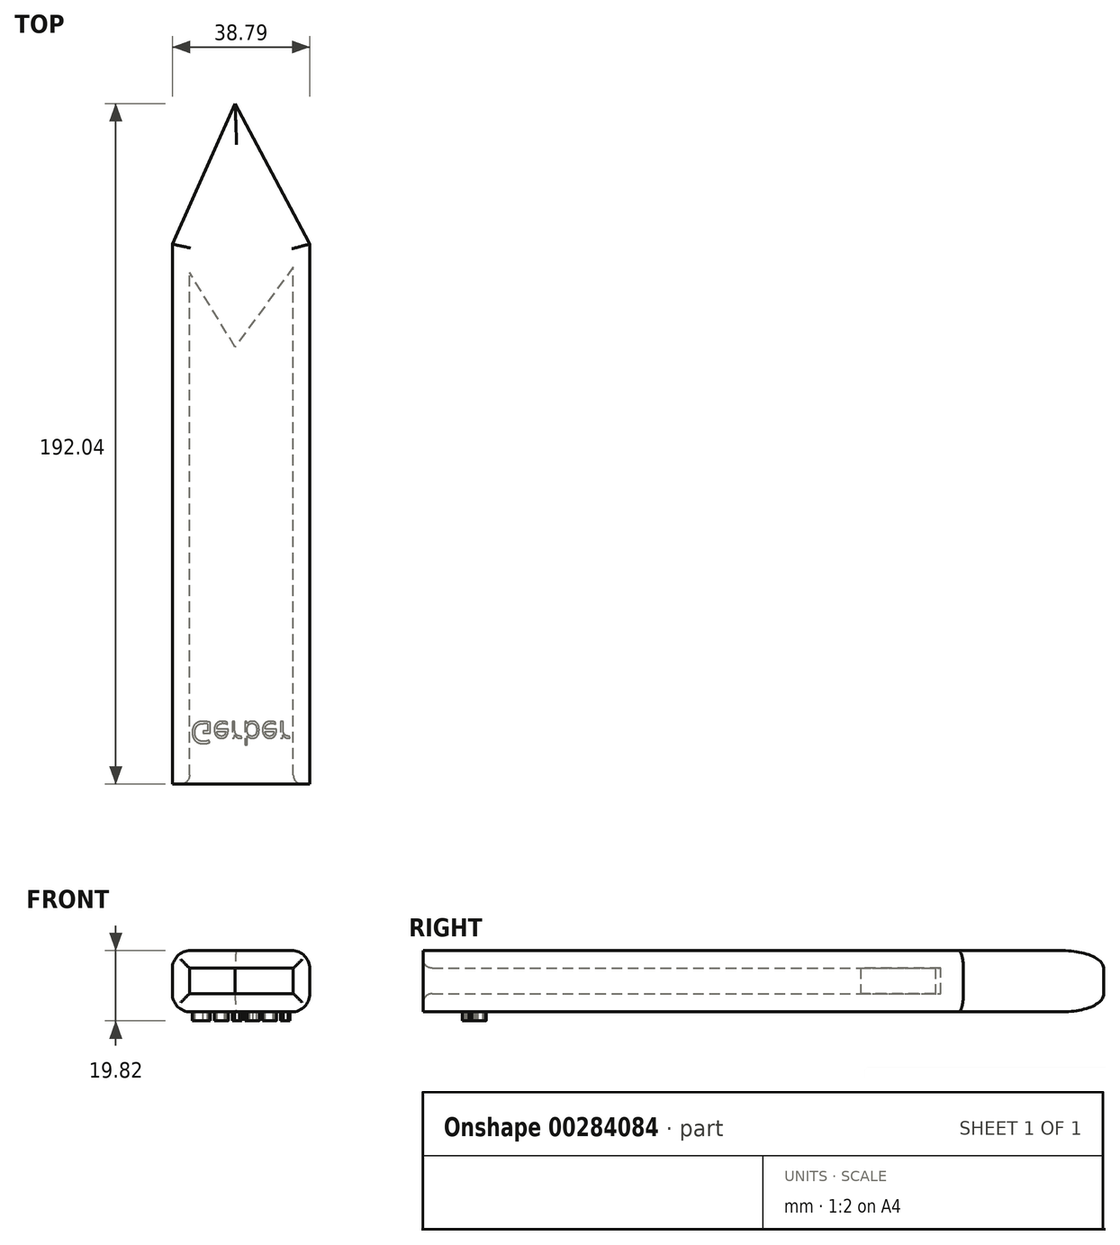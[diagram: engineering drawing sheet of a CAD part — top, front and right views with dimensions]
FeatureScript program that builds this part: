
annotation { "Feature Type Name" : "Feature", "Feature Type Description" : "" }
export const myFeature = defineFeature(function(context is Context, id is Id, definition is map)
    precondition{}
    {
        {
            var Q0;
            Q0=qCreatedBy(makeId("Front.planeOp"),FACE);
            var sketch = newSketch(context, id + "F0", { "sketchPlane" : qUnion([Q0])});
            skLineSegment(sketch, "E0", {"start": v(-12.88, 15.66) * mm, "end": v(16.4, 15.66) * mm});
            skLineSegment(sketch, "E1", {"start": v(16.4, 15.66) * mm, "end": v(16.4, 8.49) * mm});
            skLineSegment(sketch, "E2", {"start": v(16.4, 8.49) * mm, "end": v(-12.88, 8.49) * mm});
            skLineSegment(sketch, "E3", {"start": v(-12.88, 8.49) * mm, "end": v(-12.88, 15.66) * mm});
            skLineSegment(sketch, "E4", {"start": v(-17.73, 20.6) * mm, "end": v(-17.73, 3.33) * mm});
            skLineSegment(sketch, "E5", {"start": v(-17.73, 3.33) * mm, "end": v(21.06, 3.33) * mm});
            skLineSegment(sketch, "E6", {"start": v(-17.73, 20.6) * mm, "end": v(21.06, 20.6) * mm});
            skLineSegment(sketch, "E7", {"start": v(21.06, 3.33) * mm, "end": v(21.06, 20.6) * mm});
            skSolve(sketch);
        }
        {
            var Q0;
            Q0 = qSketchRegion(id + "F0", true);
            extrude(context, id + "F1", {"entities" : qUnion([Q0]), "depth" : 152.4 * mm});
        }
        {
            var Q0;
            Q0=makeQuery(id+"F1.opExtrude","CAP_EDGE",EDGE,{"disambiguationData":[OSD([sQuery(id+"F0.wireOp",EDGE,"E2")])],"isStart":false});
            var Q1;
            Q1=makeQuery(id+"F1.opExtrude","CAP_EDGE",EDGE,{"disambiguationData":[OSD([sQuery(id+"F0.wireOp",EDGE,"E1")])],"isStart":false});
            var Q2;
            Q2=makeQuery(id+"F1.opExtrude","CAP_EDGE",EDGE,{"disambiguationData":[OSD([sQuery(id+"F0.wireOp",EDGE,"E0")])],"isStart":false});
            var Q3;
            Q3=makeQuery(id+"F1.opExtrude","CAP_EDGE",EDGE,{"disambiguationData":[OSD([sQuery(id+"F0.wireOp",EDGE,"E3")])],"isStart":false});
            fillet(context, id + "F2", {"entities" : qUnion([Q0, Q1, Q2, Q3]), "radius" : 2.54 * mm, "tangentPropagation" : true, "allowEdgeOverflow" : false});
        }
        {
            var Q0;
            Q0=makeQuery(id+"F1.opExtrude","CAP_FACE",FACE,{"disambiguationData":[OSD([sQuery(id+"F0.wireOp",EDGE,"E0"),sQuery(id+"F0.wireOp",EDGE,"E1"),sQuery(id+"F0.wireOp",EDGE,"E2"),sQuery(id+"F0.wireOp",EDGE,"E3"),sQuery(id+"F0.wireOp",EDGE,"E4"),sQuery(id+"F0.wireOp",EDGE,"E5"),sQuery(id+"F0.wireOp",EDGE,"E6"),sQuery(id+"F0.wireOp",EDGE,"E7")])],"isStart":true});
            var sketch = newSketch(context, id + "F3", { "sketchPlane" : qUnion([Q0])});
            skLineSegment(sketch, "E8", {"start": v(12.65, 3.33) * mm, "end": v(12.65, 20.6) * mm});
            skLineSegment(sketch, "E9", {"start": v(12.65, 20.6) * mm, "end": v(-15.98, 20.6) * mm});
            skLineSegment(sketch, "E10", {"start": v(-15.98, 20.6) * mm, "end": v(-15.98, 3.33) * mm});
            skLineSegment(sketch, "E11", {"start": v(-15.98, 3.33) * mm, "end": v(12.65, 3.33) * mm});
            skSolve(sketch);
        }
        {
            var Q0;
            Q0 = qSketchRegion(id + "F3", true);
            extrude(context, id + "F4", {"entities" : qUnion([Q0]), "operationType" : NewBodyOperationType.ADD, "oppositeDirection" : true, "depth" : 0.5 * mm});
        }
        {
            var Q0;
            Q0=makeQuery(id+"F1.opExtrude","SWEPT_FACE",FACE,{"disambiguationData":[OSD([sQuery(id+"F0.wireOp",EDGE,"E5")])]});
            var sketch = newSketch(context, id + "F5", { "sketchPlane" : qUnion([Q0])});
            skLineSegment(sketch, "E12", {"start": v(-17.73, 0) * mm, "end": v(0, -39.64) * mm});
            skLineSegment(sketch, "E13", {"start": v(0, -39.64) * mm, "end": v(21.06, 0) * mm});
            skLineSegment(sketch, "E14", {"start": v(-17.73, 0) * mm, "end": v(0, 29) * mm});
            skLineSegment(sketch, "E15", {"start": v(0, 29) * mm, "end": v(21.06, 0) * mm});
            skSolve(sketch);
        }
        {
            var Q0;
            Q0 = qSketchRegion(id + "F5", true);
            extrude(context, id + "F6", {"entities" : qUnion([Q0]), "operationType" : NewBodyOperationType.ADD, "oppositeDirection" : true, "depth" : 17.27 * mm});
        }
        {
            var Q0;
            Q0=makeQuery(id+"F6.opExtrude","CAP_EDGE",EDGE,{"disambiguationData":[OSD([sQuery(id+"F5.wireOp",EDGE,"E12")])],"isStart":true});
            var Q1;
            Q1=makeQuery(id+"F6.opExtrude","CAP_EDGE",EDGE,{"disambiguationData":[OSD([sQuery(id+"F5.wireOp",EDGE,"E13")])],"isStart":true});
            var Q2;
            Q2=makeQuery(id+"F1.opExtrude","SWEPT_EDGE",EDGE,{"disambiguationData":[OSD([sQuery(id+"F0.wireOp",EDGE,"E5"),sQuery(id+"F0.wireOp",EDGE,"E7")])]});
            var Q3;
            Q3=makeQuery(id+"F1.opExtrude","SWEPT_EDGE",EDGE,{"disambiguationData":[OSD([sQuery(id+"F0.wireOp",EDGE,"E4"),sQuery(id+"F0.wireOp",EDGE,"E5")])]});
            fillet(context, id + "F7", {"entities" : qUnion([Q0, Q1, Q2, Q3]), "radius" : 5.08 * mm, "tangentPropagation" : true, "allowEdgeOverflow" : false});
        }
        {
            var Q0;
            Q0=makeQuery(id+"F1.opExtrude","SWEPT_EDGE",EDGE,{"disambiguationData":[OSD([sQuery(id+"F0.wireOp",EDGE,"E6"),sQuery(id+"F0.wireOp",EDGE,"E7")])]});
            var Q1;
            Q1=makeQuery(id+"F6.opExtrude","CAP_EDGE",EDGE,{"disambiguationData":[OSD([sQuery(id+"F5.wireOp",EDGE,"E13")])],"isStart":false});
            var Q2;
            Q2=makeQuery(id+"F6.opExtrude","CAP_EDGE",EDGE,{"disambiguationData":[OSD([sQuery(id+"F5.wireOp",EDGE,"E12")])],"isStart":false});
            var Q3;
            Q3=makeQuery(id+"F1.opExtrude","SWEPT_EDGE",EDGE,{"disambiguationData":[OSD([sQuery(id+"F0.wireOp",EDGE,"E4"),sQuery(id+"F0.wireOp",EDGE,"E6")])]});
            fillet(context, id + "F8", {"entities" : qUnion([Q0, Q1, Q2, Q3]), "radius" : 5.08 * mm, "tangentPropagation" : true, "allowEdgeOverflow" : false});
        }
        {
            var Q0;
            Q0=makeQuery(id+"F6.boolean.opBoolean","MERGE",FACE,{"derivedFrom":[makeQuery(id+"F1.opExtrude","SWEPT_FACE",FACE,{"disambiguationData":[OSD([sQuery(id+"F0.wireOp",EDGE,"E5")])]}),makeQuery(id+"F6.opExtrude","CAP_FACE",FACE,{"disambiguationData":[OSD([sQuery(id+"F5.wireOp",EDGE,"E12"),sQuery(id+"F5.wireOp",EDGE,"E13"),sQuery(id+"F5.wireOp",EDGE,"E14"),sQuery(id+"F5.wireOp",EDGE,"E15")])],"isStart":true})]});
            var sketch = newSketch(context, id + "F9", { "sketchPlane" : qUnion([Q0])});
            skText(sketch, "E16", { "text": "Gerber", "fontName": "OpenSans-Regular.ttf"});
            const initialGuessF9  = {"E16": [-0.01265, 0.13476, 1, 0, 0.0062]};
            skSetInitialGuess(sketch, initialGuessF9);
            skSolve(sketch);
        }
        {
            var Q0;
            Q0 = qSketchRegion(id + "F9", true);
            extrude(context, id + "F10", {"entities" : qUnion([Q0]), "operationType" : NewBodyOperationType.ADD, "depth" : 2.54 * mm});
        }
    });
